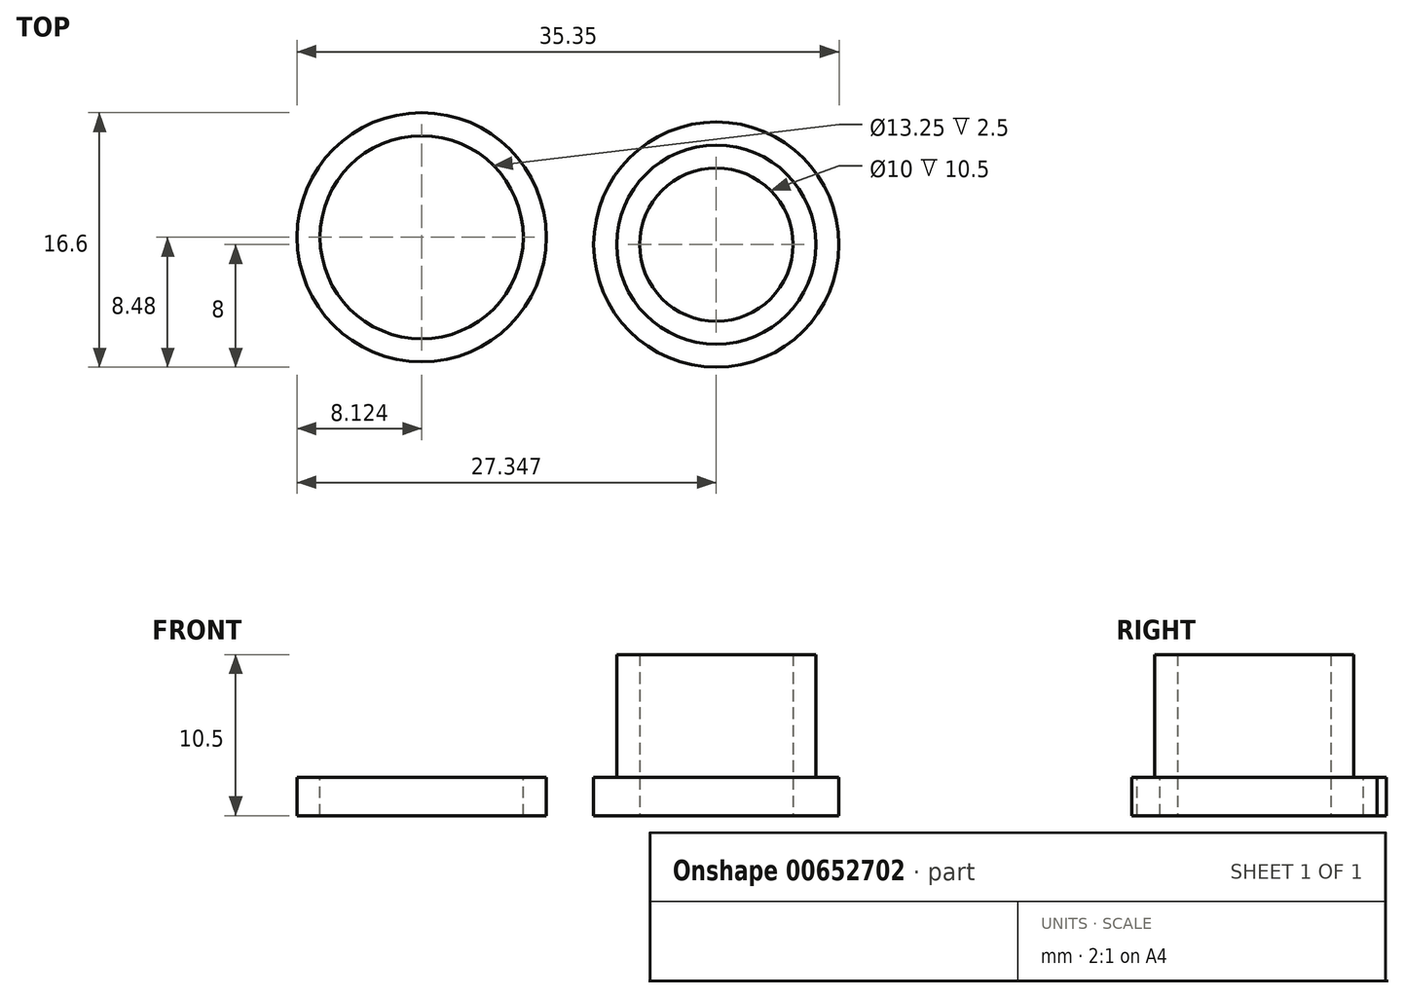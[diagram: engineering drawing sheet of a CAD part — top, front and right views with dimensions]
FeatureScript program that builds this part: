
annotation { "Feature Type Name" : "Feature", "Feature Type Description" : "" }
export const myFeature = defineFeature(function(context is Context, id is Id, definition is map)
    precondition{}
    {
        {
            var Q0;
            Q0=qCreatedBy(makeId("Top.planeOp"),FACE);
            var sketch = newSketch(context, id + "F0", { "sketchPlane" : qUnion([Q0]), "disableImprinting" : false});
            skCircle(sketch, "E0", {"center": v(-68.9, 5.85) * mm, "radius": 6.5 * mm});
            skCircle(sketch, "E1", {"center": v(-68.9, 5.85) * mm, "radius": 5 * mm});
            skCircle(sketch, "E2", {"center": v(-68.9, 5.85) * mm, "radius": 8 * mm});
            skCircle(sketch, "E3", {"center": v(-88.13, 6.33) * mm, "radius": 6.62 * mm});
            skCircle(sketch, "E4", {"center": v(-88.13, 6.33) * mm, "radius": 8.12 * mm});
            skSolve(sketch);
        }
        {
            var Q0;
            Q0=makeQuery(id+"F0.imprint","IMPRINT",FACE,{"disambiguationData":[TD([[makeQuery(id+"F0.imprint","IMPRINT",EDGE,{"derivedFrom":sQuery(id+"F0.wireOp",EDGE,"E0")}),1.0]])]});
            extrude(context, id + "F1", {"entities" : qUnion([Q0]), "depth" : 8 * mm, "offsetDistance" : 25 * mm});
        }
        {
            var Q0;
            Q0=makeQuery(id+"F0.imprint","IMPRINT",FACE,{"disambiguationData":[TD([[makeQuery(id+"F0.imprint","IMPRINT",EDGE,{"derivedFrom":sQuery(id+"F0.wireOp",EDGE,"E0")}),1.0]])]});
            var Q1;
            Q1=makeQuery(id+"F0.imprint","IMPRINT",FACE,{"disambiguationData":[TD([[makeQuery(id+"F0.imprint","IMPRINT",EDGE,{"derivedFrom":sQuery(id+"F0.wireOp",EDGE,"E0")}),-1.0]])]});
            extrude(context, id + "F2", {"entities" : qUnion([Q0, Q1]), "operationType" : NewBodyOperationType.ADD, "oppositeDirection" : true, "depth" : 2.5 * mm, "offsetDistance" : 25 * mm});
        }
        {
            var Q0;
            Q0=makeQuery(id+"F0.imprint","IMPRINT",FACE,{"disambiguationData":[TD([[makeQuery(id+"F0.imprint","IMPRINT",EDGE,{"derivedFrom":sQuery(id+"F0.wireOp",EDGE,"E3")}),-1.0]])]});
            extrude(context, id + "F3", {"entities" : qUnion([Q0]), "oppositeDirection" : true, "depth" : 2.5 * mm, "offsetDistance" : 25 * mm});
        }
    });
